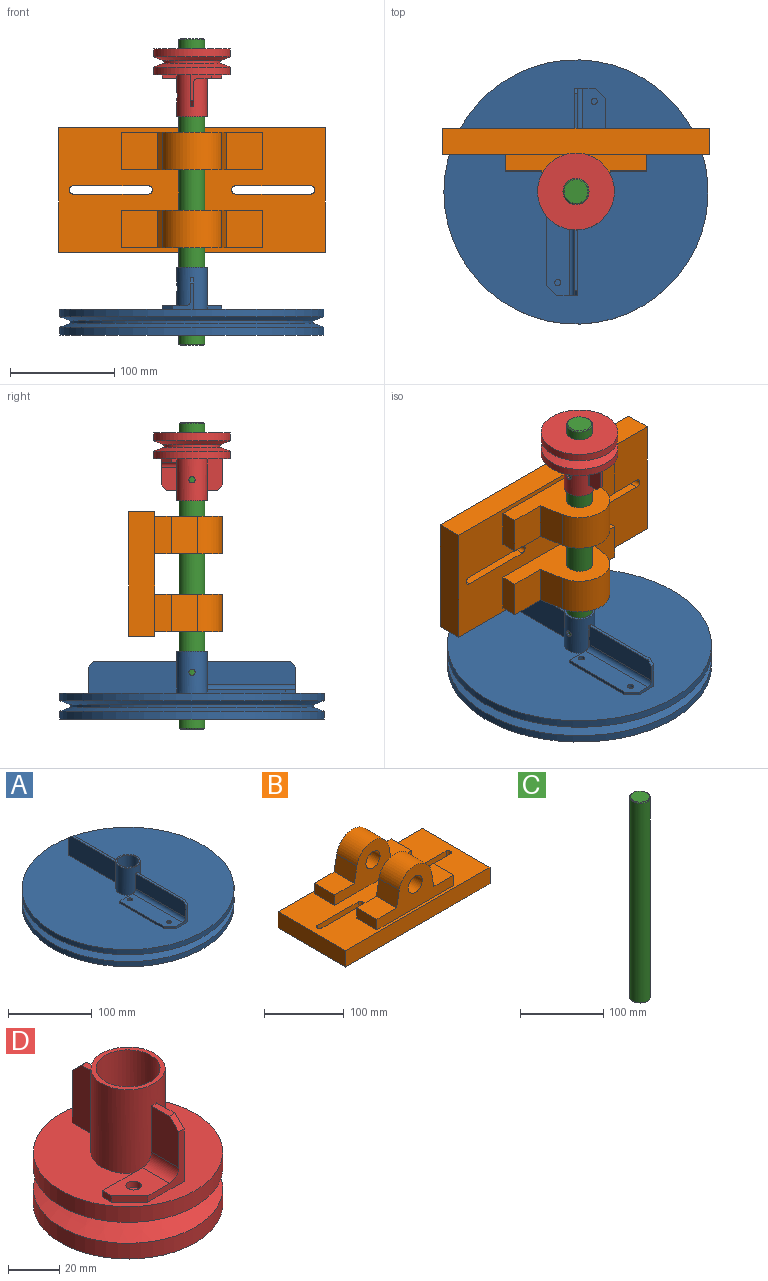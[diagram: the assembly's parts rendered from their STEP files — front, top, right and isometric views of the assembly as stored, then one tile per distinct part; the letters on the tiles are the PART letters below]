
ASSEMBLY  parts=4 mates=3
PART A: 41 faces, bbox 254x254x65 mm
  f0: plane 254x254mm, normal (0,0,1), area 45010.4mm2, adj f1,f8,f9,f10,f14,f15,f19,f21
  f1: cylinder r=127mm len=254mm, axis (0,0,1), area 5984.7mm2, adj f0,f2
  f2: cone r=127mm half-angle=70deg, axis (0,0,1), area 8157.4mm2, adj f1,f3
  f3: cylinder r=117mm len=234mm, axis (0,0,1), area 2000mm2, adj f2,f4
  f4: cone r=127mm half-angle=70deg, axis (0,0,-1), area 8157.4mm2, adj f3,f5
  f5: cylinder r=127mm len=254mm, axis (0,0,1), area 5984.7mm2, adj f4,f6
  f6: plane 254x254mm, normal (0,0,-1), area 50179.9mm2, adj f5,f7
  f7: cylinder r=12.5mm len=65mm, axis (0,0,1), area 5076.6mm2, adj f6,f35,f36
  f8: plane 30x27.3mm, normal (0,-1,0), area 95.3mm2, adj f0,f11,f12,f13,f14,f16,f21
  f9: plane 30x0.3mm, normal (0,-1,0), area 8.9mm2, adj f0,f10,f11,f21
  f10: plane 85x30mm, normal (-1,0,0), area 2537.5mm2, adj f0,f9,f11,f15,f20
  f11: plane 80x3mm, normal (0,0,1), area 239.9mm2, adj f8,f9,f10,f12,f20,f21
  f12: plane 85x22mm, normal (1,0,0), area 1857.5mm2, adj f8,f11,f15,f16,f20
  f13: plane 85x22mm, normal (0,0,1), area 1763.5mm2, adj f8,f14,f15,f16,f17,f18,f19
  f14: plane 75x3mm, normal (1,0,0), area 225mm2, adj f0,f8,f13,f19
  f15: plane 25x20mm, normal (0,1,0), area 131.4mm2, adj f0,f10,f12,f13,f16,f19,f20
  f16: cylinder r=5mm len=85mm, axis (0,1,0), area 667.6mm2, adj f8,f12,f13,f15
  f17: cylinder r=3mm len=6mm, axis (0,0,1), area 56.5mm2, adj f13,f38
  f18: cylinder r=3mm len=6mm, axis (0,0,1), area 56.5mm2, adj f13,f39
  f19: plane 10x10mm, normal (0.71,0.71,0), area 42.4mm2, adj f0,f13,f14,f15
  f20: plane 5x5mm, normal (0,0.71,0.71), area 21.2mm2, adj f10,f11,f12,f15
  f21: cylinder r=14.5mm len=40mm, axis (0,0,-1), area 3471.2mm2, adj f0,f8,f9,f11,f22,f23,f25,f35
  f22: plane 30x27.3mm, normal (0,1,0), area 95.3mm2, adj f0,f21,f25,f26,f27,f28,f30
  f23: plane 30x0.3mm, normal (0,1,0), area 8.9mm2, adj f0,f21,f24,f25
  f24: plane 85x30mm, normal (1,0,0), area 2537.5mm2, adj f0,f23,f25,f29,f34
  f25: plane 80x3mm, normal (0,0,1), area 239.9mm2, adj f21,f22,f23,f24,f26,f34
  f26: plane 85x22mm, normal (-1,0,0), area 1857.5mm2, adj f22,f25,f29,f30,f34
  f27: plane 85x22mm, normal (0,0,1), area 1763.5mm2, adj f22,f28,f29,f30,f31,f32,f33
  f28: plane 75x3mm, normal (-1,0,0), area 225mm2, adj f0,f22,f27,f33
  f29: plane 25x20mm, normal (0,-1,0), area 131.4mm2, adj f0,f24,f26,f27,f30,f33,f34
  f30: cylinder r=5mm len=85mm, axis (0,-1,0), area 667.6mm2, adj f22,f26,f27,f29
  f31: cylinder r=3mm len=6mm, axis (0,0,1), area 56.5mm2, adj f27,f40
  f32: cylinder r=3mm len=6mm, axis (0,0,1), area 56.5mm2, adj f27,f37
  f33: plane 10x10mm, normal (-0.71,-0.71,0), area 42.4mm2, adj f0,f27,f28,f29
  f34: plane 5x5mm, normal (0,-0.71,0.71), area 21.2mm2, adj f24,f25,f26,f29
  f35: plane 29x29mm, normal (0,0,1), area 169.6mm2, adj f7,f21
  f36: cylinder r=3mm len=6mm, axis (-1,0,0), area 38.2mm2, adj f7,f21
  f37: plane 6x6mm, normal (0,0,1), area 28.3mm2, adj f32
  f38: plane 6x6mm, normal (0,0,1), area 28.3mm2, adj f17
  f39: plane 6x6mm, normal (0,0,1), area 28.3mm2, adj f18
  f40: plane 6x6mm, normal (0,0,1), area 28.3mm2, adj f31
PART B: 34 faces, bbox 256x120x90 mm
  f0: plane 36x35.03mm, normal (0,0,1), area 1260.9mm2, adj f1,f6,f8,f9
  f1: plane 36x16mm, normal (-1,0,0), area 576mm2, adj f0,f8,f9,f10
  f2: plane 36x16mm, normal (1,0,0), area 576mm2, adj f3,f8,f9,f10
  f3: plane 36x35.03mm, normal (0,0,1), area 1260.9mm2, adj f2,f4,f8,f9
  f4: plane 36x25.04mm, normal (0.98,0,0.17), area 915.2mm2, adj f3,f5,f8,f9
  f5: cylinder r=29mm len=57.12mm, axis (0,-1,0), area 2915.4mm2, adj f4,f6,f8,f9
  f6: plane 36x25.04mm, normal (-0.98,0,0.17), area 915.2mm2, adj f0,f5,f8,f9
  f7: cylinder r=12.5mm len=36mm, axis (0,-1,0), area 2827.4mm2, adj f8,f9
  f8: plane 136x65mm, normal (0,1,0), area 4256.1mm2, adj f0,f1,f2,f3,f4,f5,f6,f7
  f9: plane 136x65mm, normal (0,-1,0), area 4256.1mm2, adj f0,f1,f2,f3,f4,f5,f6,f7
  f10: plane 256x120mm, normal (0,0,1), area 19675.5mm2, adj f1,f2,f8,f9,f12,f13,f19,f20
  f11: plane 36x35.03mm, normal (0,0,1), area 1260.9mm2, adj f12,f17,f19,f20
  f12: plane 36x16mm, normal (-1,0,0), area 576mm2, adj f10,f11,f19,f20
  f13: plane 36x16mm, normal (1,0,0), area 576mm2, adj f10,f14,f19,f20
  f14: plane 36x35.03mm, normal (0,0,1), area 1260.9mm2, adj f13,f15,f19,f20
  f15: plane 36x25.04mm, normal (0.98,0,0.17), area 915.2mm2, adj f14,f16,f19,f20
  f16: cylinder r=29mm len=57.12mm, axis (0,-1,0), area 2915.4mm2, adj f15,f17,f19,f20
  f17: plane 36x25.04mm, normal (-0.98,0,0.17), area 915.2mm2, adj f11,f16,f19,f20
  f18: cylinder r=12.5mm len=36mm, axis (0,-1,0), area 2827.4mm2, adj f19,f20
  f19: plane 136x65mm, normal (0,1,0), area 4256.1mm2, adj f10,f11,f12,f13,f14,f15,f16,f17
  f20: plane 136x65mm, normal (0,-1,0), area 4256.1mm2, adj f10,f11,f12,f13,f14,f15,f16,f17
  f21: cylinder r=4mm len=25mm, axis (0,0,1), area 314.2mm2, adj f10,f22,f32,f33
  f22: plane 72x25mm, normal (0,-1,0), area 1800mm2, adj f10,f21,f23,f33
  f23: cylinder r=4mm len=25mm, axis (0,0,1), area 314.2mm2, adj f10,f22,f32,f33
  f24: plane 72x25mm, normal (0,-1,0), area 1800mm2, adj f10,f25,f30,f33
  f25: cylinder r=4mm len=25mm, axis (0,0,1), area 314.2mm2, adj f10,f24,f26,f33
  f26: plane 72x25mm, normal (0,1,0), area 1800mm2, adj f10,f25,f30,f33
  f27: plane 120x25mm, normal (1,0,0), area 3000mm2, adj f10,f28,f31,f33
  f28: plane 256x25mm, normal (0,-1,0), area 6400mm2, adj f10,f27,f29,f33
  f29: plane 120x25mm, normal (-1,0,0), area 3000mm2, adj f10,f28,f31,f33
  f30: cylinder r=4mm len=25mm, axis (0,0,1), area 314.2mm2, adj f10,f24,f26,f33
  f31: plane 256x25mm, normal (0,1,0), area 6400mm2, adj f10,f27,f29,f33
  f32: plane 72x25mm, normal (0,1,0), area 1800mm2, adj f10,f21,f23,f33
  f33: plane 256x120mm, normal (0,0,-1), area 29467.5mm2, adj f21,f22,f23,f24,f25,f26,f27,f28
PART C: 5 faces, bbox 25x25x295 mm
  f0: cylinder r=12.5mm len=293mm, axis (0,0,-1), area 23012.2mm2, adj f3,f4
  f1: plane 23x23mm, normal (0,0,1), area 415.5mm2, adj f3
  f2: plane 23x23mm, normal (0,0,-1), area 415.5mm2, adj f4
  f3: cone r=11.5mm half-angle=45deg, axis (0,0,-1), area 106.6mm2, adj f0,f1
  f4: cone r=12.5mm half-angle=45deg, axis (0,0,1), area 106.6mm2, adj f0,f2
PART D: 37 faces, bbox 74x74x65 mm
  f0: plane 74x74mm, normal (0,0,1), area 2840.5mm2, adj f1,f8,f9,f10,f14,f15,f18,f20
  f1: cylinder r=37mm len=74mm, axis (0,0,1), area 1743.6mm2, adj f0,f2
  f2: cone r=37mm half-angle=70deg, axis (0,0,1), area 2139.7mm2, adj f1,f3
  f3: cylinder r=27mm len=54mm, axis (0,0,1), area 461.5mm2, adj f2,f4
  f4: cone r=37mm half-angle=70deg, axis (0,0,-1), area 2139.7mm2, adj f3,f5
  f5: cylinder r=37mm len=74mm, axis (0,0,1), area 1743.6mm2, adj f4,f6
  f6: plane 74x74mm, normal (0,0,-1), area 3810mm2, adj f5,f7
  f7: cylinder r=12.5mm len=65mm, axis (0,0,1), area 5076.6mm2, adj f6,f33,f34
  f8: plane 30x27.3mm, normal (0,-1,0), area 95.3mm2, adj f0,f11,f12,f13,f14,f16,f20
  f9: plane 30x0.3mm, normal (0,-1,0), area 8.9mm2, adj f0,f10,f11,f20
  f10: plane 30x15mm, normal (-1,0,0), area 437.5mm2, adj f0,f9,f11,f15,f19
  f11: plane 10x3mm, normal (0,0,1), area 29.9mm2, adj f8,f9,f10,f12,f19,f20
  f12: plane 22x15mm, normal (1,0,0), area 317.5mm2, adj f8,f11,f15,f16,f19
  f13: plane 22x15mm, normal (0,0,1), area 251.7mm2, adj f8,f14,f15,f16,f17,f18
  f14: plane 5x3mm, normal (1,0,0), area 15mm2, adj f0,f8,f13,f18
  f15: plane 25x20mm, normal (0,1,0), area 131.4mm2, adj f0,f10,f12,f13,f16,f18,f19
  f16: cylinder r=5mm len=15mm, axis (0,1,0), area 117.8mm2, adj f8,f12,f13,f15
  f17: cylinder r=3mm len=6mm, axis (0,0,1), area 56.5mm2, adj f13,f35
  f18: plane 10x10mm, normal (0.71,0.71,0), area 42.4mm2, adj f0,f13,f14,f15
  f19: plane 5x5mm, normal (0,0.71,0.71), area 21.2mm2, adj f10,f11,f12,f15
  f20: cylinder r=14.5mm len=40mm, axis (0,0,-1), area 3471.2mm2, adj f0,f8,f9,f11,f21,f22,f24,f33
  f21: plane 30x27.3mm, normal (0,1,0), area 95.3mm2, adj f0,f20,f24,f25,f26,f27,f29
  f22: plane 30x0.3mm, normal (0,1,0), area 8.9mm2, adj f0,f20,f23,f24
  f23: plane 30x15mm, normal (1,0,0), area 437.5mm2, adj f0,f22,f24,f28,f32
  f24: plane 10x3mm, normal (0,0,1), area 29.9mm2, adj f20,f21,f22,f23,f25,f32
  f25: plane 22x15mm, normal (-1,0,0), area 317.5mm2, adj f21,f24,f28,f29,f32
  f26: plane 22x15mm, normal (0,0,1), area 251.7mm2, adj f21,f27,f28,f29,f30,f31
  f27: plane 5x3mm, normal (-1,0,0), area 15mm2, adj f0,f21,f26,f31
  f28: plane 25x20mm, normal (0,-1,0), area 131.4mm2, adj f0,f23,f25,f26,f29,f31,f32
  f29: cylinder r=5mm len=15mm, axis (0,-1,0), area 117.8mm2, adj f21,f25,f26,f28
  f30: cylinder r=3mm len=6mm, axis (0,0,1), area 56.5mm2, adj f26,f36
  f31: plane 10x10mm, normal (-0.71,-0.71,0), area 42.4mm2, adj f0,f26,f27,f28
  f32: plane 5x5mm, normal (0,-0.71,0.71), area 21.2mm2, adj f23,f24,f25,f28
  f33: plane 29x29mm, normal (0,0,1), area 169.6mm2, adj f7,f20
  f34: cylinder r=3mm len=6mm, axis (-1,0,0), area 38.2mm2, adj f7,f20
  f35: plane 6x6mm, normal (0,0,1), area 28.3mm2, adj f17
  f36: plane 6x6mm, normal (0,0,1), area 28.3mm2, adj f30
PLACE A rot(axis=(0,0,-1),180deg) t=(-226.11,67.55,-11.72)mm
PLACE B rot(axis=(0,-0.71,0.71),180deg) t=(-226.11,67.55,108.28)mm
PLACE C rot(axis=(0,-1,0),180deg) t=(-226.11,67.55,273.28)mm
PLACE D rot(axis=(0,-1,0),180deg) t=(-226.11,67.55,263.28)mm
MATE fastened B.f7 <-> D.f20  axis (0,0,1) through (-226.11,67.55,183.28)mm
MATE fastened A.f1 <-> C.f0  axis (0,0,-1) through (-226.11,67.55,-11.72)mm
MATE fastened D.f7 <-> C.f0  axis (0,0,1) through (-226.11,67.55,263.28)mm
